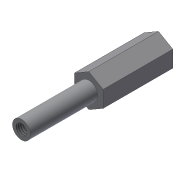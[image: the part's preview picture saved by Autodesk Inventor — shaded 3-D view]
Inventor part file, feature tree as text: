
AUTODESK INVENTOR PART (.ipt)
format: ipt  version: 2018 (Build 220112000, 112)  size: 90,624 bytes
history: native  units: mm
features: sketch x3, extrude x2, hole x1
ambient origin geometry x8: Origin, YZ Plane, XZ Plane, XY Plane, X Axis, Y Axis, Z Axis, Center Point
bodies: Solid1 (feature_tree)
feature tree (6):
  extrude  "Extrusion1"  Depth=31.0mm TaperAngle=0.0deg
  extrude  "Extrusion2"  Depth=30.0mm TaperAngle=0.0deg
  hole  "Hole1"  [1 undecoded]
  sketch  "Sketch1"  dims[d0=12.7mm d1=31.0mm d2=0.0mm]
  sketch  "Sketch2"  dims[d3=8.0mm d4=30.0mm d5=0.0mm]
  sketch  "Sketch3"  dims[d6=4.917mm d7=12.0mm d8=4.0mm d9=2.0mm d10=90.0deg d11=17.1mm d12=20.594885mm]
note: 1 required parameter value undecoded (feature->parameter linkage not recoverable at this tier; creation-order binding heuristic only, values carry confidence <= 0.55)
